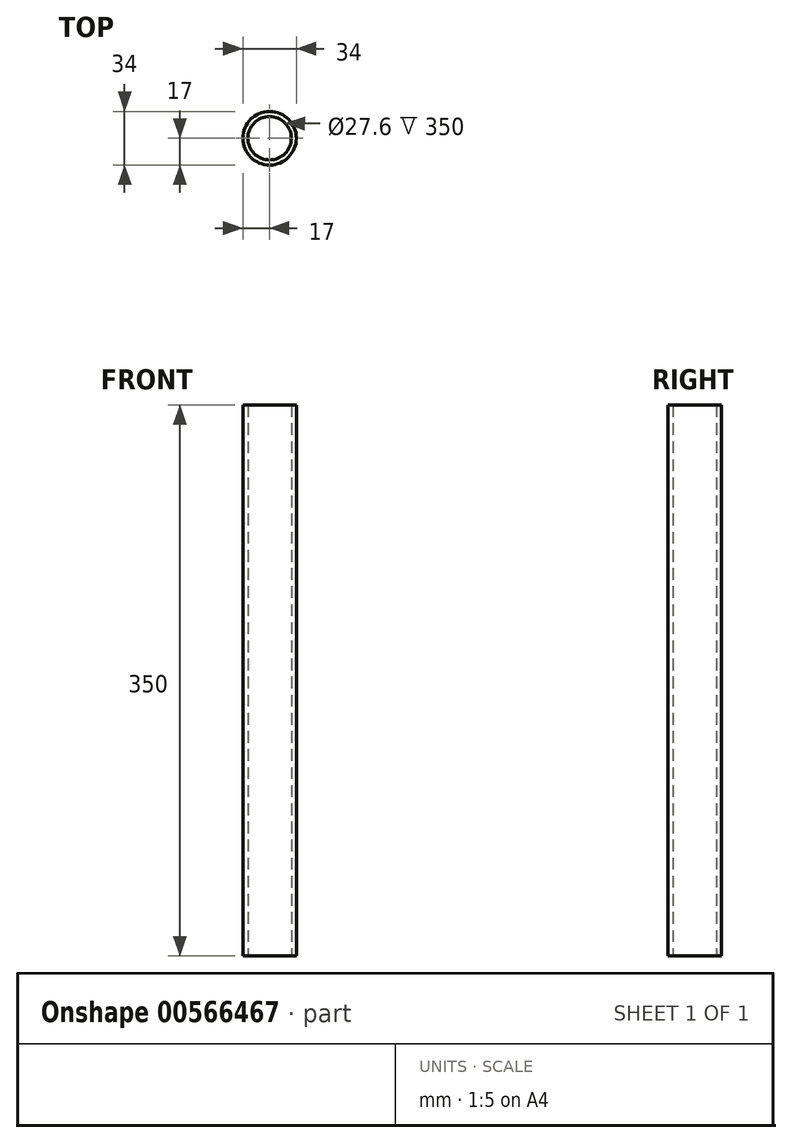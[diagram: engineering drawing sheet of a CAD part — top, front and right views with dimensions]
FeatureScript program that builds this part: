
annotation { "Feature Type Name" : "Feature", "Feature Type Description" : "" }
export const myFeature = defineFeature(function(context is Context, id is Id, definition is map)
    precondition{}
    {
        {
            var Q0;
            Q0=qCreatedBy(makeId("Top.planeOp"),FACE);
            var sketch = newSketch(context, id + "F0", { "sketchPlane" : qUnion([Q0])});
            skCircle(sketch, "E0", {"center": v(0, 0) * mm, "radius": 13.8 * mm});
            skCircle(sketch, "E1", {"center": v(0, 0) * mm, "radius": 17 * mm});
            skSolve(sketch);
        }
        {
            var Q0;
            Q0=qSketchRegion(id+"F0",true);
            extrude(context, id + "F1", {"entities" : qUnion([Q0]), "depth" : 350 * mm, "offsetDistance" : 25 * mm});
        }
    });
